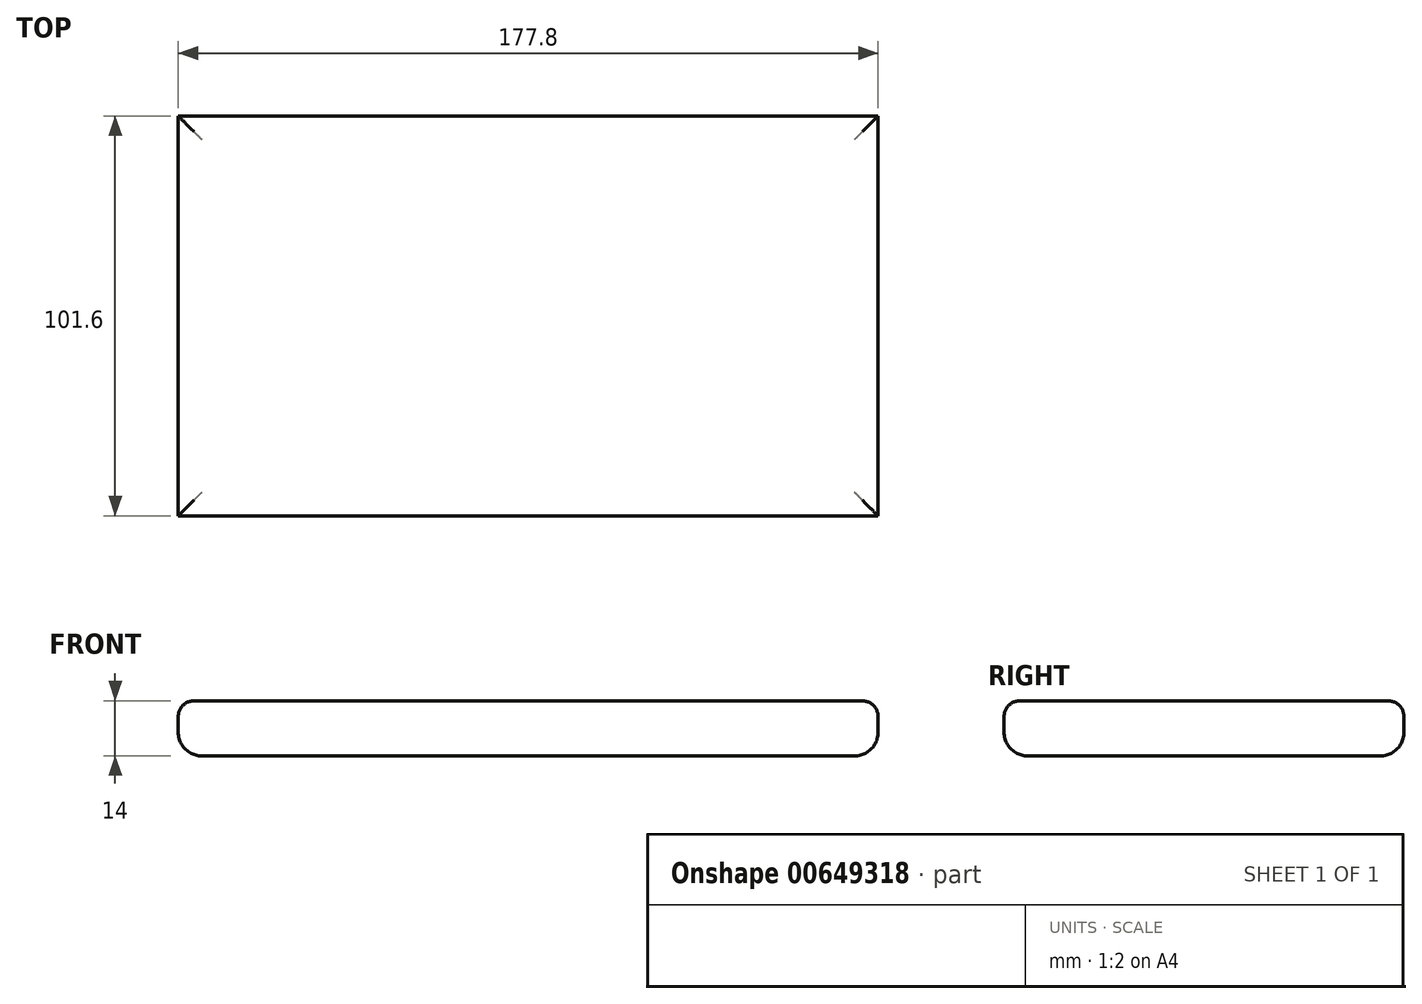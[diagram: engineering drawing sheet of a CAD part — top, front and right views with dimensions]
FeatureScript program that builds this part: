
annotation { "Feature Type Name" : "Feature", "Feature Type Description" : "" }
export const myFeature = defineFeature(function(context is Context, id is Id, definition is map)
    precondition{}
    {
        {
            var Q0;
            Q0=qCreatedBy(makeId("Top.planeOp"),FACE);
            var sketch = newSketch(context, id + "F0", { "sketchPlane" : qUnion([Q0])});
            skLineSegment(sketch, "E0.bottom", {"start": v(-58.3, 50.6) * mm, "end": v(119.5, 50.6) * mm});
            skLineSegment(sketch, "E0.top", {"start": v(-58.3, -51) * mm, "end": v(119.5, -51) * mm});
            skLineSegment(sketch, "E0.left", {"start": v(-58.3, 50.6) * mm, "end": v(-58.3, -51) * mm});
            skLineSegment(sketch, "E0.right", {"start": v(119.5, 50.6) * mm, "end": v(119.5, -51) * mm});
            skSolve(sketch);
        }
        {
            var Q0;
            Q0 = qSketchRegion(id + "F0", true);
            extrude(context, id + "F1", {"entities" : qUnion([Q0]), "depth" : 14 * mm, "offsetDistance" : 25 * mm});
        }
        {
            var Q0;
            Q0=makeQuery(id+"F1.opExtrude","CAP_EDGE",EDGE,{"disambiguationData":[OSD([sQuery(id+"F0.wireOp",EDGE,"E0.left")])],"isStart":false});
            var Q1;
            Q1=makeQuery(id+"F1.opExtrude","CAP_EDGE",EDGE,{"disambiguationData":[OSD([sQuery(id+"F0.wireOp",EDGE,"E0.bottom")])],"isStart":false});
            var Q2;
            Q2=makeQuery(id+"F1.opExtrude","CAP_EDGE",EDGE,{"disambiguationData":[OSD([sQuery(id+"F0.wireOp",EDGE,"E0.top")])],"isStart":false});
            var Q3;
            Q3=makeQuery(id+"F1.opExtrude","CAP_EDGE",EDGE,{"disambiguationData":[OSD([sQuery(id+"F0.wireOp",EDGE,"E0.right")])],"isStart":false});
            fillet(context, id + "F2", {"entities" : qUnion([Q0, Q1, Q2, Q3]), "radius" : 4 * mm, "tangentPropagation" : true, "allowEdgeOverflow" : false});
        }
        {
            var Q0;
            Q0=makeQuery(id+"F1.opExtrude","CAP_EDGE",EDGE,{"disambiguationData":[OSD([sQuery(id+"F0.wireOp",EDGE,"E0.left")])],"isStart":true});
            var Q1;
            Q1=makeQuery(id+"F1.opExtrude","CAP_EDGE",EDGE,{"disambiguationData":[OSD([sQuery(id+"F0.wireOp",EDGE,"E0.bottom")])],"isStart":true});
            var Q2;
            Q2=makeQuery(id+"F1.opExtrude","CAP_EDGE",EDGE,{"disambiguationData":[OSD([sQuery(id+"F0.wireOp",EDGE,"E0.top")])],"isStart":true});
            var Q3;
            Q3=makeQuery(id+"F1.opExtrude","CAP_EDGE",EDGE,{"disambiguationData":[OSD([sQuery(id+"F0.wireOp",EDGE,"E0.right")])],"isStart":true});
            fillet(context, id + "F3", {"entities" : qUnion([Q0, Q1, Q2, Q3]), "radius" : 6 * mm, "tangentPropagation" : true, "allowEdgeOverflow" : false});
        }
    });
